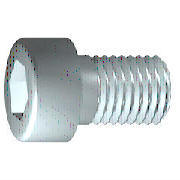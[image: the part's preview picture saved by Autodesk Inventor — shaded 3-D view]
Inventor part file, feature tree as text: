
AUTODESK INVENTOR PART (.ipt)
format: ipt  version: 2020 (Build 240168000, 168)  size: 199,168 bytes
history: native  units: mm (DEFAULTED — no unit token found)
features: sketch x2, extrude x1, plane x1, fillet x1
ambient origin geometry x7: Origin, YZ Plane, XY Plane, X Axis, Y Axis, Z Axis, Center Point
bodies: Solid1 (feature_tree), Body (feature_tree)
feature tree (5):
  extrude  "Slot"  Depth=3.5mm
  plane  "Work Plane1"
  fillet  "Fillet2"  Radius=3.5mm
  sketch  "Sketch1"  dims[d1=13.6mm d2=0.49086mm d3=3.5mm]
  sketch  "Sketch2"  dims[d4=2.7mm d5=60.0deg d6=5.0mm d7=5.0mm d8=3.464102mm d9=8.5mm d10=90.0deg d11=10.0mm d12=0.0mm d13=13.6mm d14=0.0mm d15=0.49076mm d16=0.49076mm d17=0.5mm d19=0.0mm d26=16.0mm d27=45.0deg d28=0.0mm d29=0.0mm d30=0.1mm]
